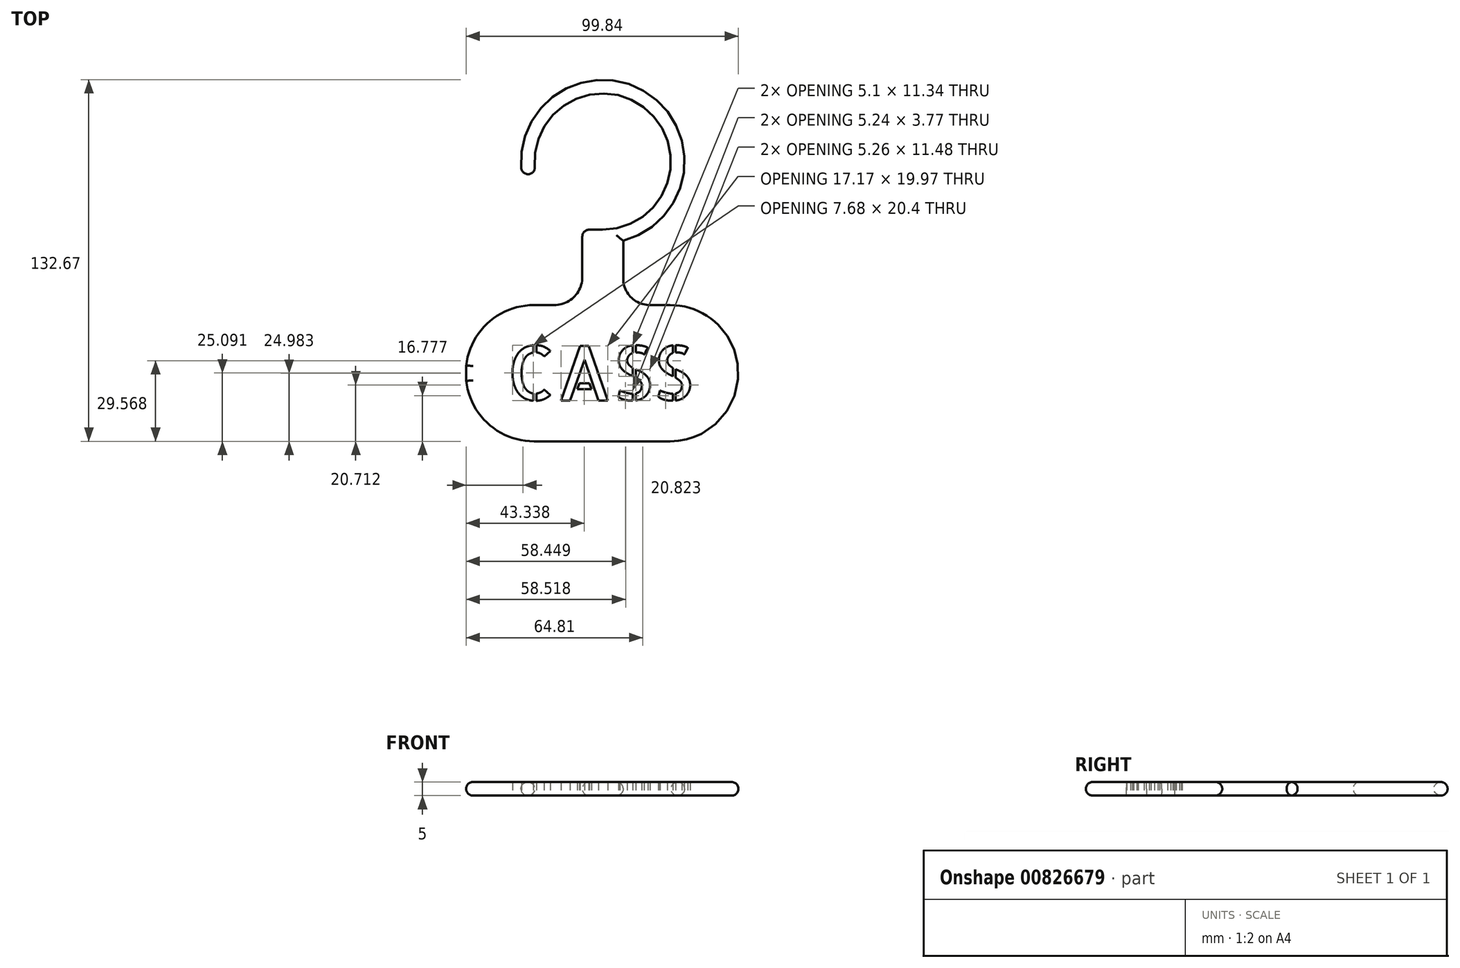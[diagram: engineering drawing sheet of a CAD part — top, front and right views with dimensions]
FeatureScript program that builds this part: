
annotation { "Feature Type Name" : "Feature", "Feature Type Description" : "" }
export const myFeature = defineFeature(function(context is Context, id is Id, definition is map)
    precondition{}
    {
        {
            var Q0;
            Q0=qCreatedBy(makeId("Top.planeOp"),FACE);
            var sketch = newSketch(context, id + "F0", { "sketchPlane" : qUnion([Q0])});
            skLineSegment(sketch, "E0.bottom", {"start": v(-25, 0) * mm, "end": v(-17.5, 0) * mm});
            skLineSegment(sketch, "E0.top", {"start": v(-25, -50) * mm, "end": v(25, -50) * mm});
            skLineSegment(sketch, "E0.left", {"start": v(-50, -25) * mm, "end": v(-50, -25) * mm});
            skLineSegment(sketch, "E0.right", {"start": v(50, -25) * mm, "end": v(50, -25) * mm});
            skLineSegment(sketch, "E1.left", {"start": v(-7.24, 10.26) * mm, "end": v(-7.24, 23.67) * mm});
            skLineSegment(sketch, "E1.right", {"start": v(7.76, 9.74) * mm, "end": v(7.76, 23.67) * mm});
            skLineSegment(sketch, "E2.trimOffspring", {"start": v(17.5, 0) * mm, "end": v(25, 0) * mm});
            skPoint(sketch, "E3.visualSharp", {"position": v(-50, 0) * mm});
            skArc(sketch, "E3.filletArc", {"start": v(-25, 0) * mm, "mid": v(-42.68, -7.32) * mm, "end": v(-50, -25) * mm});
            skPoint(sketch, "E4.visualSharp", {"position": v(-50, -50) * mm});
            skArc(sketch, "E4.filletArc", {"start": v(-50, -25) * mm, "mid": v(-42.68, -42.68) * mm, "end": v(-25, -50) * mm});
            skPoint(sketch, "E5.visualSharp", {"position": v(50, -50) * mm});
            skArc(sketch, "E5.filletArc", {"start": v(25, -50) * mm, "mid": v(42.68, -42.68) * mm, "end": v(50, -25) * mm});
            skPoint(sketch, "E6.visualSharp", {"position": v(50, 0) * mm});
            skArc(sketch, "E6.filletArc", {"start": v(50, -25) * mm, "mid": v(42.68, -7.32) * mm, "end": v(25, 0) * mm});
            skArc(sketch, "E7", {"start": v(-17.5, 0) * mm, "mid": v(-10.25, 3) * mm, "end": v(-7.24, 10.26) * mm});
            skArc(sketch, "E8", {"start": v(7.76, 9.74) * mm, "mid": v(10.6, 2.85) * mm, "end": v(17.5, 0) * mm});
            skLineSegment(sketch, "E9", {"start": v(0.26, 27.67) * mm, "end": v(0.26, 52.67) * mm, "construction": true});
            skArc(sketch, "E10", {"start": v(7.76, 23.62) * mm, "mid": v(17.69, 77.08) * mm, "end": v(-29.65, 50.33) * mm});
            skArc(sketch, "E11", {"start": v(0.26, 27.67) * mm, "mid": v(17.23, 71.02) * mm, "end": v(-24.67, 50.72) * mm});
            skLineSegment(sketch, "E12.bottom", {"start": v(-26.73, 48.06) * mm, "end": v(-26.73, 48.06) * mm});
            skLineSegment(sketch, "E13", {"start": v(0.26, 27.67) * mm, "end": v(-4.74, 27.67) * mm});
            skLineSegment(sketch, "E14", {"start": v(-7.24, 25.17) * mm, "end": v(-7.24, 23.67) * mm});
            skPoint(sketch, "E15", {"position": v(-26.85, 48.04) * mm});
            skPoint(sketch, "E16.orphan", {"position": v(0.26, 23.67) * mm});
            skLineSegment(sketch, "E17.right", {"start": v(-49.84, -22.2) * mm, "end": v(-49.84, -27.8) * mm});
            skPoint(sketch, "E18.visualSharp", {"position": v(-109.88, 39.1) * mm});
            skPoint(sketch, "E19.visualSharp", {"position": v(-29.31, 47.6) * mm});
            skArc(sketch, "E19.filletArc", {"start": v(-29.65, 50.33) * mm, "mid": v(-28.7, 48.55) * mm, "end": v(-26.73, 48.06) * mm});
            skPoint(sketch, "E20.visualSharp", {"position": v(-24.4, 48.47) * mm});
            skArc(sketch, "E20.filletArc", {"start": v(-26.73, 48.06) * mm, "mid": v(-25.18, 49) * mm, "end": v(-24.67, 50.72) * mm});
            skPoint(sketch, "E21.visualSharp", {"position": v(-7.24, 27.67) * mm});
            skArc(sketch, "E21.filletArc", {"start": v(-4.74, 27.67) * mm, "mid": v(-6.51, 26.94) * mm, "end": v(-7.24, 25.17) * mm});
            skSolve(sketch);
        }
        {
            var Q0;
            {var subQ4=sQuery(id+"F0.wireOp",EDGE,"E0.bottom");Q0=makeQuery(id+"F0.imprint","IMPRINT",FACE,{"disambiguationData":[TD([[makeQuery(id+"F0.imprint","IMPRINT",EDGE,{"derivedFrom":subQ4}),-1.0]])]});}
            extrude(context, id + "F1", {"entities" : qUnion([Q0]), "depth" : 5 * mm, "offsetDistance" : 25 * mm});
        }
        {
            var Q0;
            Q0=makeQuery(id+"F1.opExtrude","CAP_EDGE",EDGE,{"disambiguationData":[OSD([sQuery(id+"F0.wireOp",EDGE,"E11")])],"isStart":false});
            var Q1;
            Q1=makeQuery(id+"F1.opExtrude","CAP_EDGE",EDGE,{"disambiguationData":[OSD([sQuery(id+"F0.wireOp",EDGE,"E11")])],"isStart":true});
            var Q2;
            Q2=makeQuery(id+"F1.opExtrude","CAP_EDGE",EDGE,{"disambiguationData":[OSD([sQuery(id+"F0.wireOp",EDGE,"E10")])],"isStart":false});
            var Q3;
            Q3=makeQuery(id+"F1.opExtrude","CAP_EDGE",EDGE,{"disambiguationData":[OSD([sQuery(id+"F0.wireOp",EDGE,"E13")])],"isStart":false});
            var Q4;
            Q4=makeQuery(id+"F1.opExtrude","CAP_EDGE",EDGE,{"disambiguationData":[OSD([sQuery(id+"F0.wireOp",EDGE,"E21.filletArc")])],"isStart":false});
            var Q5;
            Q5=makeQuery(id+"F1.opExtrude","CAP_EDGE",EDGE,{"disambiguationData":[OSD([sQuery(id+"F0.wireOp",EDGE,"E19.filletArc"),sQuery(id+"F0.wireOp",EDGE,"E20.filletArc")])],"isStart":false});
            var Q6;
            Q6=makeQuery(id+"F1.opExtrude","CAP_EDGE",EDGE,{"disambiguationData":[OSD([sQuery(id+"F0.wireOp",EDGE,"E19.filletArc"),sQuery(id+"F0.wireOp",EDGE,"E20.filletArc")])],"isStart":true});
            var Q7;
            Q7=makeQuery(id+"F1.opExtrude","CAP_EDGE",EDGE,{"disambiguationData":[OSD([sQuery(id+"F0.wireOp",EDGE,"E1.left"),sQuery(id+"F0.wireOp",EDGE,"E14")])],"isStart":false});
            var Q8;
            Q8=makeQuery(id+"F1.opExtrude","CAP_EDGE",EDGE,{"disambiguationData":[OSD([sQuery(id+"F0.wireOp",EDGE,"E7")])],"isStart":false});
            var Q9;
            Q9=makeQuery(id+"F1.opExtrude","CAP_EDGE",EDGE,{"disambiguationData":[OSD([sQuery(id+"F0.wireOp",EDGE,"E3.filletArc")])],"isStart":false});
            var Q10;
            Q10=makeQuery(id+"F1.opExtrude","CAP_EDGE",EDGE,{"disambiguationData":[OSD([sQuery(id+"F0.wireOp",EDGE,"E0.bottom")])],"isStart":false});
            var Q11;
            Q11=makeQuery(id+"F1.opExtrude","CAP_EDGE",EDGE,{"disambiguationData":[OSD([sQuery(id+"F0.wireOp",EDGE,"E4.filletArc")])],"isStart":false});
            var Q12;
            Q12=makeQuery(id+"F1.opExtrude","CAP_FACE",FACE,{"disambiguationData":[OSD([sQuery(id+"F0.wireOp",EDGE,"E0.bottom"),sQuery(id+"F0.wireOp",EDGE,"E0.top"),sQuery(id+"F0.wireOp",EDGE,"E1.left"),sQuery(id+"F0.wireOp",EDGE,"E1.right"),sQuery(id+"F0.wireOp",EDGE,"E2.trimOffspring"),sQuery(id+"F0.wireOp",EDGE,"E3.filletArc"),sQuery(id+"F0.wireOp",EDGE,"E4.filletArc"),sQuery(id+"F0.wireOp",EDGE,"E5.filletArc"),sQuery(id+"F0.wireOp",EDGE,"E6.filletArc"),sQuery(id+"F0.wireOp",EDGE,"E7"),sQuery(id+"F0.wireOp",EDGE,"E8"),sQuery(id+"F0.wireOp",EDGE,"E10"),sQuery(id+"F0.wireOp",EDGE,"E11"),sQuery(id+"F0.wireOp",EDGE,"E13"),sQuery(id+"F0.wireOp",EDGE,"E14"),sQuery(id+"F0.wireOp",EDGE,"E17.right"),sQuery(id+"F0.wireOp",EDGE,"E19.filletArc"),sQuery(id+"F0.wireOp",EDGE,"E20.filletArc"),sQuery(id+"F0.wireOp",EDGE,"E21.filletArc")])],"isStart":false});
            var Q13;
            Q13=makeQuery(id+"F1.opExtrude","CAP_EDGE",EDGE,{"disambiguationData":[OSD([sQuery(id+"F0.wireOp",EDGE,"E17.right")])],"isStart":false});
            var Q14;
            Q14=makeQuery(id+"F1.opExtrude","CAP_FACE",FACE,{"disambiguationData":[OSD([sQuery(id+"F0.wireOp",EDGE,"E0.bottom"),sQuery(id+"F0.wireOp",EDGE,"E0.top"),sQuery(id+"F0.wireOp",EDGE,"E1.left"),sQuery(id+"F0.wireOp",EDGE,"E1.right"),sQuery(id+"F0.wireOp",EDGE,"E2.trimOffspring"),sQuery(id+"F0.wireOp",EDGE,"E3.filletArc"),sQuery(id+"F0.wireOp",EDGE,"E4.filletArc"),sQuery(id+"F0.wireOp",EDGE,"E5.filletArc"),sQuery(id+"F0.wireOp",EDGE,"E6.filletArc"),sQuery(id+"F0.wireOp",EDGE,"E7"),sQuery(id+"F0.wireOp",EDGE,"E8"),sQuery(id+"F0.wireOp",EDGE,"E10"),sQuery(id+"F0.wireOp",EDGE,"E11"),sQuery(id+"F0.wireOp",EDGE,"E13"),sQuery(id+"F0.wireOp",EDGE,"E14"),sQuery(id+"F0.wireOp",EDGE,"E17.right"),sQuery(id+"F0.wireOp",EDGE,"E19.filletArc"),sQuery(id+"F0.wireOp",EDGE,"E20.filletArc"),sQuery(id+"F0.wireOp",EDGE,"E21.filletArc")])],"isStart":true});
            fillet(context, id + "F2", {"entities" : qUnion([Q0, Q1, Q2, Q3, Q4, Q5, Q6, Q7, Q8, Q9, Q10, Q11, Q12, Q13, Q14]), "radius" : 2.5 * mm, "tangentPropagation" : true, "allowEdgeOverflow" : false});
        }
        {
            var Q0;
            Q0=qCreatedBy(makeId("Top.planeOp"),FACE);
            var sketch = newSketch(context, id + "F3", { "sketchPlane" : qUnion([Q0])});
            skLineSegment(sketch, "E22", {"start": v(0, 0) * mm, "end": v(0, -50) * mm, "construction": true});
            skLineSegment(sketch, "E23", {"start": v(0, -50) * mm, "end": v(0, -5) * mm, "construction": true});
            skLineSegment(sketch, "E24", {"start": v(0, -50) * mm, "end": v(0, -45) * mm, "construction": true});
            skLineSegment(sketch, "E25", {"start": v(0, -45) * mm, "end": v(-30, -45) * mm, "construction": true});
            skLineSegment(sketch, "E26", {"start": v(0, -5) * mm, "end": v(-30, -5) * mm});
            skLineSegment(sketch, "E27", {"start": v(0, -5) * mm, "end": v(30, -5) * mm, "construction": true});
            skLineSegment(sketch, "E28", {"start": v(0, -45) * mm, "end": v(30, -45) * mm, "construction": true});
            skLineSegment(sketch, "E29", {"start": v(-30, -5) * mm, "end": v(-30, -15) * mm, "construction": true});
            skLineSegment(sketch, "E30", {"start": v(-30, -15) * mm, "end": v(-30, -35) * mm, "construction": true});
            skLineSegment(sketch, "E31", {"start": v(-30, -15) * mm, "end": v(-35, -15) * mm, "construction": true});
            skLineSegment(sketch, "E32", {"start": v(-30, -35) * mm, "end": v(-35, -35) * mm, "construction": true});
            skText(sketch, "E33", { "text": "CASS", "fontName": "AllertaStencil-Regular.ttf"});
            const initialGuessF3  = {"E33": [-0.035, -0.035, 1, 0, 0.02]};
            skSetInitialGuess(sketch, initialGuessF3);
            skSolve(sketch);
        }
        {
            var Q0;
            Q0 = qSketchRegion(id + "F3", true);
            extrude(context, id + "F4", {"entities" : qUnion([Q0]), "operationType" : NewBodyOperationType.REMOVE, "depth" : 25.4 * mm, "offsetDistance" : 25 * mm});
        }
    });
